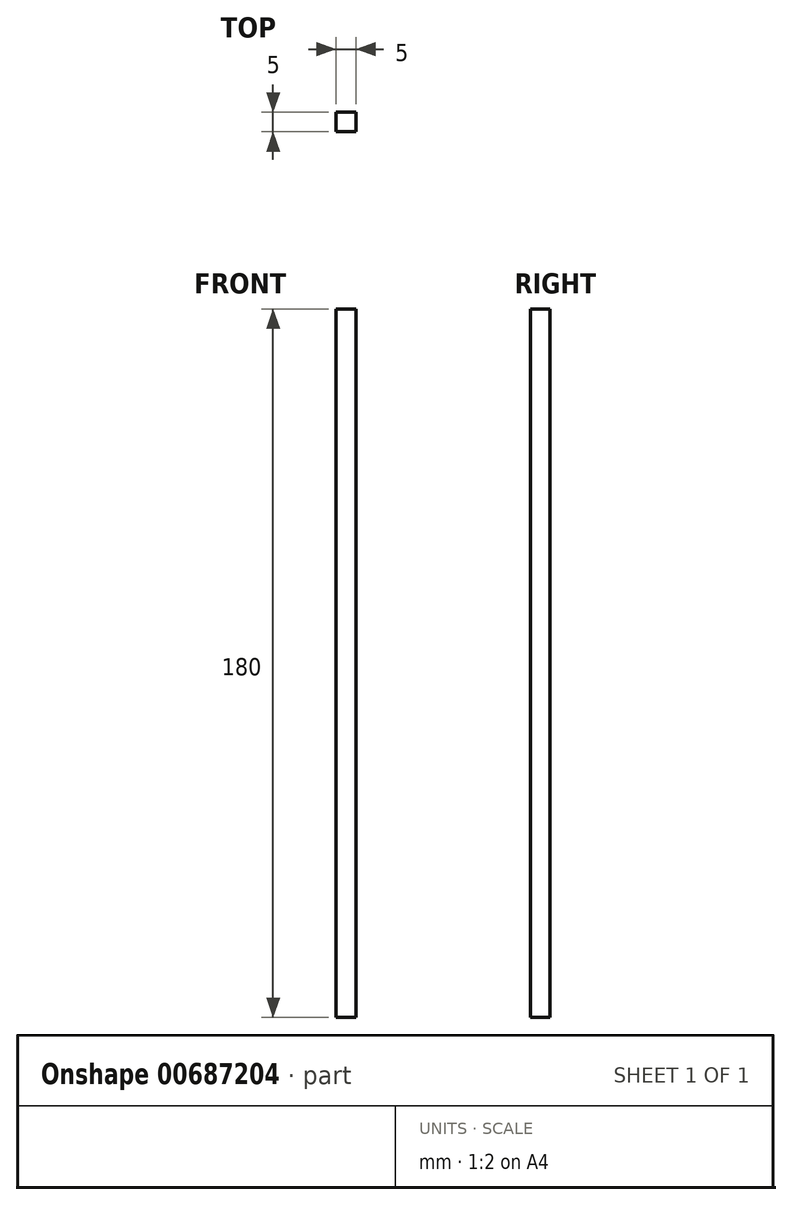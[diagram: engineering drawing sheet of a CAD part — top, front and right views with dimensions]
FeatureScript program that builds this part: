
annotation { "Feature Type Name" : "Feature", "Feature Type Description" : "" }
export const myFeature = defineFeature(function(context is Context, id is Id, definition is map)
    precondition{}
    {
        {
            var Q0;
            Q0=qCreatedBy(makeId("Front.planeOp"),FACE);
            var sketch = newSketch(context, id + "F0", { "sketchPlane" : qUnion([Q0])});
            skLineSegment(sketch, "E0.bottom", {"start": v(-13.18, 0) * mm, "end": v(-8.18, 0) * mm});
            skLineSegment(sketch, "E0.top", {"start": v(-13.18, 180) * mm, "end": v(-8.18, 180) * mm});
            skLineSegment(sketch, "E0.left", {"start": v(-13.18, 0) * mm, "end": v(-13.18, 180) * mm});
            skLineSegment(sketch, "E0.right", {"start": v(-8.18, 0) * mm, "end": v(-8.18, 180) * mm});
            skSolve(sketch);
        }
        {
            var Q0;
            Q0 = qSketchRegion(id + "F0", true);
            extrude(context, id + "F1", {"entities" : qUnion([Q0]), "depth" : 5 * mm, "offsetDistance" : 25 * mm});
        }
    });
